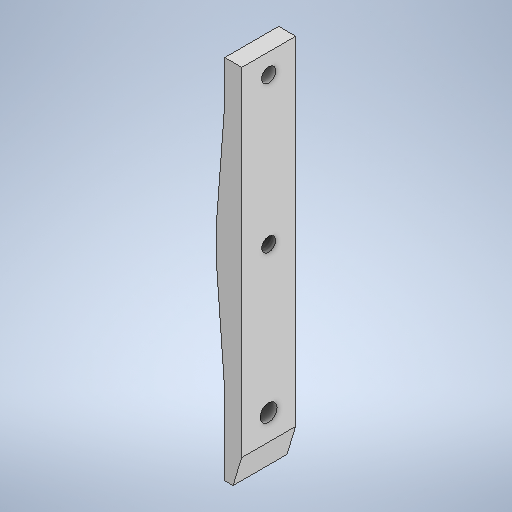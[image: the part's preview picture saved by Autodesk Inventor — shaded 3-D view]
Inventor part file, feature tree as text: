
AUTODESK INVENTOR PART (.ipt)
format: ipt  version: 2025.1 (Build 291241000, 241)  size: 283,136 bytes
history: native  units: mm
features: sketch x3, hole x3, extrude x1
ambient origin geometry x8: Origin, YZ Plane, XZ Plane, XY Plane, X Axis, Y Axis, Z Axis, Center Point
bodies: Volumenkörper1 (feature_tree)
feature tree (7):
  extrude  "Extrusion1"  Depth=3.0mm
  sketch  "Skizze3"  dims[d3=3.0mm d7=19.0mm d8=0.0mm]
  hole  "Bohrung1"  [1 undecoded]
  hole  "Bohrung2"  [1 undecoded]
  hole  "Bohrung3"  [1 undecoded]
  sketch  "Skizze1"  dims[d0=10.0mm d1=3.0mm]
  sketch  "Skizze5"  dims[d17=119.0mm d19=6.0mm d21=9.5mm d22=19.0mm d23=7.0mm d25=5.0mm d26=6.0mm d27=4.0mm d28=2.0mm d29=90.0deg d30=8.0mm d31=20.594885mm d32=6.0mm d33=6.0mm d34=4.0mm d35=2.0mm d36=90.0deg d37=8.0mm d38=0.0mm d42=14.0mm d43=39.0mm d44=10.0mm d45=39.0mm d46=5.0mm d47=9.5mm d48=4.917mm d49=12.0mm d50=4.0mm d51=2.0mm d52=90.0deg d53=8.0mm d54=0.0mm]
note: 3 required parameter values undecoded (feature->parameter linkage not recoverable at this tier; creation-order binding heuristic only, values carry confidence <= 0.55)
